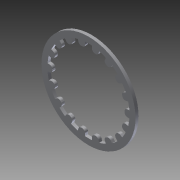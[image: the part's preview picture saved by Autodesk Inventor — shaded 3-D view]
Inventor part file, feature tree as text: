
AUTODESK INVENTOR PART (.ipt)
format: ipt  version: 2014 (Build 180170000, 170)  size: 200,704 bytes
history: native  units: in
note: dims shown in document units (in); Inventor stores cm internally (conversion verified against a paired STEP export)
features: other x7, extrude x1, sketch x1
ambient origin geometry x8: Origin, YZ Plane, XZ Plane, XY Plane, X Axis, Y Axis, Z Axis, Center Point
bodies: Solid1 (feature_tree)
feature tree (9):
  extrude  "Extrusion1"  [1 undecoded]
  other  "lockwasher_XY"
  other  "lockwasher_YZ"
  other  "lockwasher_ZX"
  other  "lockwasher_X"
  other  "lockwasher_Y"
  other  "lockwasher_Z"
  other  "lockwasher_Center"
  sketch  "Sketch_2"  dims[d0=0.02in d1=0.0in]
note: 1 required parameter value undecoded (feature->parameter linkage not recoverable at this tier; creation-order binding heuristic only, values carry confidence <= 0.55)
